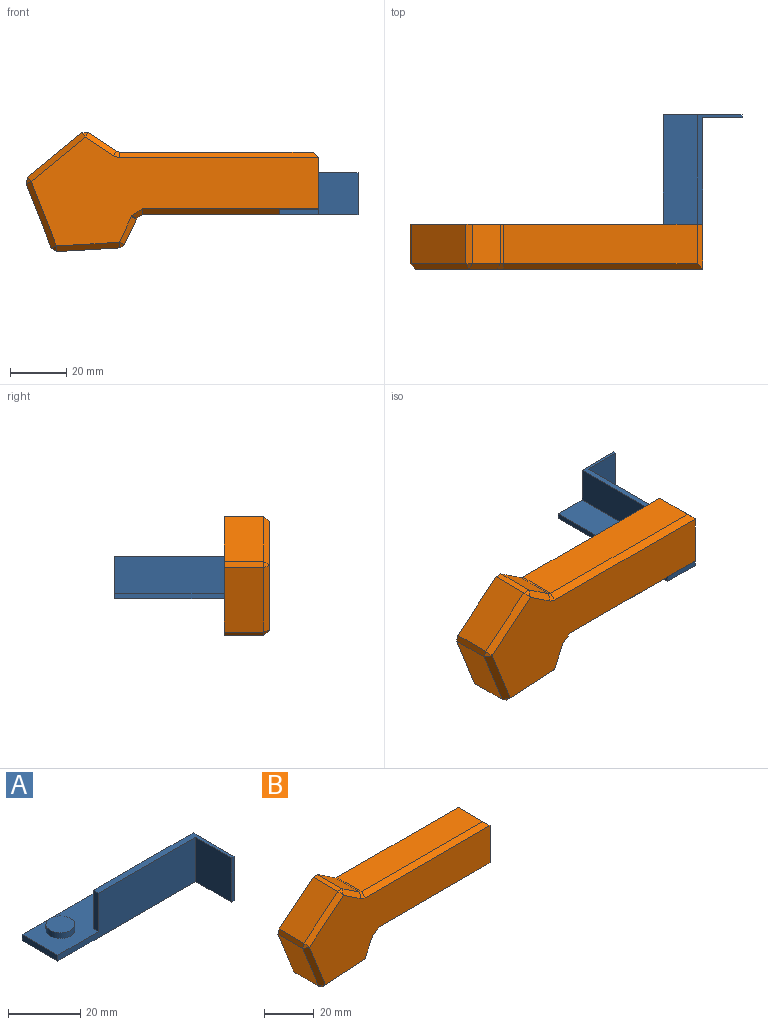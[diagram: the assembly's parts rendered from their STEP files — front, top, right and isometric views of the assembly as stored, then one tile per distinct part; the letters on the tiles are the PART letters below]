
ASSEMBLY  parts=2 mates=1
PART A: 13 faces, bbox 55x28x15 mm
  f0: plane 55x14mm, normal (0,0,1), area 641.7mm2, adj f2,f3,f4,f5,f8,f10,f11
  f1: plane 15x1mm, normal (0,-1,0), area 15mm2, adj f2,f6,f7,f12
  f2: plane 28x15mm, normal (1,0,0), area 264mm2, adj f0,f1,f3,f7,f11,f12
  f3: plane 55x2mm, normal (0,1,0), area 110mm2, adj f0,f2,f4,f7
  f4: plane 14x2mm, normal (-1,0,0), area 28mm2, adj f0,f3,f5,f7
  f5: plane 54x15mm, normal (0,-1,0), area 602mm2, adj f0,f4,f6,f7,f10,f12
  f6: plane 15x14mm, normal (-1,0,0), area 210mm2, adj f1,f5,f7,f12
  f7: plane 55x28mm, normal (0,0,-1), area 784mm2, adj f1,f2,f3,f4,f5,f6
  f8: cylinder r=4mm len=8mm, axis (0,0,-1), area 50.3mm2, adj f0,f9
  f9: plane 8x8mm, normal (0,0,1), area 50.3mm2, adj f8
  f10: plane 13x2mm, normal (-1,0,0), area 26mm2, adj f0,f5,f11,f12
  f11: plane 39x13mm, normal (0,1,0), area 507mm2, adj f0,f2,f10,f12
  f12: plane 39x16mm, normal (0,0,1), area 92mm2, adj f1,f2,f5,f6,f10,f11
PART B: 41 faces, bbox 104.2x16x42.5 mm
  f0: plane 14x9.08mm, normal (0.9,0,-0.43), area 140.6mm2, adj f1,f10,f23,f24
  f1: plane 14x0.42mm, normal (0.92,0,-0.38), area 6.3mm2, adj f0,f10,f20,f22
  f2: plane 60.83x14mm, normal (0,0,-1), area 801.4mm2, adj f10,f18,f19,f20,f40
  f3: plane 18.23x16mm, normal (1,0,0), area 291.7mm2, adj f9,f10,f18,f28
  f4: plane 68.84x14mm, normal (0,0,1), area 963.8mm2, adj f10,f28,f30,f31
  f5: plane 14x9.97mm, normal (0.56,0,0.83), area 168mm2, adj f10,f30,f36,f39
  f6: plane 19.26x15.84mm, normal (-0.64,0,0.77), area 349.1mm2, adj f10,f33,f37,f39
  f7: plane 22.96x14mm, normal (-0.93,0,-0.37), area 345.2mm2, adj f10,f27,f32,f33
  f8: plane 22.34x14mm, normal (0.06,0,-1), area 313.3mm2, adj f10,f24,f26,f27
  f9: plane 102.3x38.79mm, normal (0,-1,0), area 2227.3mm2, adj f3,f19,f21,f22,f23,f26,f31,f32
  f10: plane 104.16x42.45mm, normal (0,1,0), area 953.3mm2, adj f0,f1,f2,f3,f4,f5,f6,f7
  f11: plane 12x9mm, normal (-1,0,0), area 108mm2, adj f10,f12,f16,f17
  f12: plane 67x12mm, normal (0,0,1), area 753.7mm2, adj f10,f11,f13,f17,f40
  f13: plane 17x12mm, normal (-1,0,0), area 204mm2, adj f10,f12,f14,f17
  f14: plane 80x12mm, normal (0,0,-1), area 960mm2, adj f10,f13,f15,f17
  f15: cylinder r=13mm len=26mm, axis (0,1,0), area 490.1mm2, adj f10,f14,f16,f17
  f16: plane 13x12mm, normal (0,0,1), area 156mm2, adj f10,f11,f15,f17
  f17: plane 93x26mm, normal (0,1,0), area 1742.5mm2, adj f11,f12,f13,f14,f15,f16
  f18: plane 16x2mm, normal (0.71,0,-0.71), area 42.4mm2, adj f2,f3,f10,f19
  f19: plane 62.83x2mm, normal (0,-0.71,-0.71), area 174.9mm2, adj f2,f9,f18,f21
  f20: plane 14x1.85mm, normal (0.55,0,-0.83), area 31.1mm2, adj f1,f2,f10,f21
  f21: plane 3.69x3.23mm, normal (0.43,-0.64,-0.64), area 8.7mm2, adj f9,f19,f20,f22
  f22: plane 2x2mm, normal (0.65,-0.71,-0.27), area 1.2mm2, adj f1,f9,f21,f23
  f23: plane 9.89x6.11mm, normal (0.64,-0.71,-0.3), area 28.3mm2, adj f0,f9,f22,f25
  f24: plane 14x1.69mm, normal (0.56,0,-0.83), area 28.5mm2, adj f0,f8,f10,f25
  f25: plane 2x2mm, normal (0.42,-0.65,-0.63), area 2.7mm2, adj f23,f24,f26
  f26: plane 22.46x3.33mm, normal (0.04,-0.71,-0.71), area 63.3mm2, adj f8,f9,f25,f29
  f27: plane 14x1.98mm, normal (-0.54,0,-0.84), area 32.9mm2, adj f7,f8,f10,f29
  f28: plane 16x2mm, normal (0.71,0,0.71), area 42.4mm2, adj f3,f4,f10,f31
  f29: plane 2x2mm, normal (-0.42,-0.63,-0.66), area 3mm2, adj f26,f27,f32
  f30: plane 14x1.11mm, normal (0.29,0,0.96), area 16.3mm2, adj f4,f5,f10,f34
  f31: plane 70.84x2mm, normal (0,-0.71,0.71), area 197.5mm2, adj f4,f9,f28,f34
  f32: plane 23.69x10.87mm, normal (-0.66,-0.71,-0.26), area 69.7mm2, adj f7,f9,f29,f35
  f33: plane 14x2.28mm, normal (-0.97,0,0.25), area 32.9mm2, adj f6,f7,f10,f35
  f34: plane 2.34x2.22mm, normal (0.21,-0.69,0.69), area 4.8mm2, adj f9,f30,f31,f36
  f35: plane 2.28x2mm, normal (-0.75,-0.63,0.2), area 3mm2, adj f32,f33,f37
  f36: plane 11.09x8.34mm, normal (0.39,-0.71,0.59), area 33.9mm2, adj f5,f9,f34,f38
  f37: plane 20.53x17.38mm, normal (-0.45,-0.71,0.55), area 70.5mm2, adj f6,f9,f35,f38
  f38: plane 2.38x2mm, normal (-0.04,-0.63,0.78), area 3.1mm2, adj f36,f37,f39
  f39: plane 14x2.38mm, normal (-0.05,0,1), area 33.4mm2, adj f5,f6,f10,f38
  f40: cylinder r=4mm len=8mm, axis (0,0,-1), area 62mm2, adj f2,f12
PLACE A rot(axis=(0,0,1),90deg) t=(149.32,-58.79,-27.29)mm
PLACE B rot(axis=(0.15,0.13,0.98),0deg) t=(31.98,-16,-20.76)mm
MATE cylindrical A.f8 <-> B.f40  axis (0,0,1) through (105.98,-23,-23.29)mm
